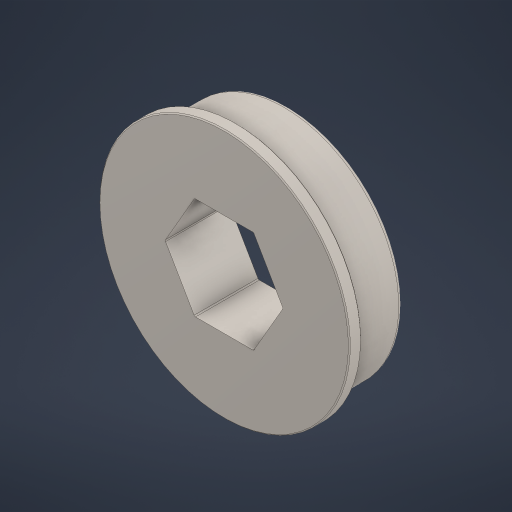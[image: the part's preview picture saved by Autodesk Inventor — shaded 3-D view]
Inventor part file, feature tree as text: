
AUTODESK INVENTOR PART (.ipt)
format: ipt  version: 2024 (Build 280153000, 153)  size: 244,736 bytes
history: native  units: in
note: dims shown in document units (in); Inventor stores cm internally (conversion verified against a paired STEP export)
features: fillet x1
ambient origin geometry x8: Origin, YZ Plane, XZ Plane, XY Plane, X Axis, Y Axis, Z Axis, Center Point
bodies: Solid1 (feature_tree)
feature tree (1):
  fillet  "Fillet2"  [1 undecoded]
note: 1 required parameter value undecoded (feature->parameter linkage not recoverable at this tier; creation-order binding heuristic only, values carry confidence <= 0.55)
